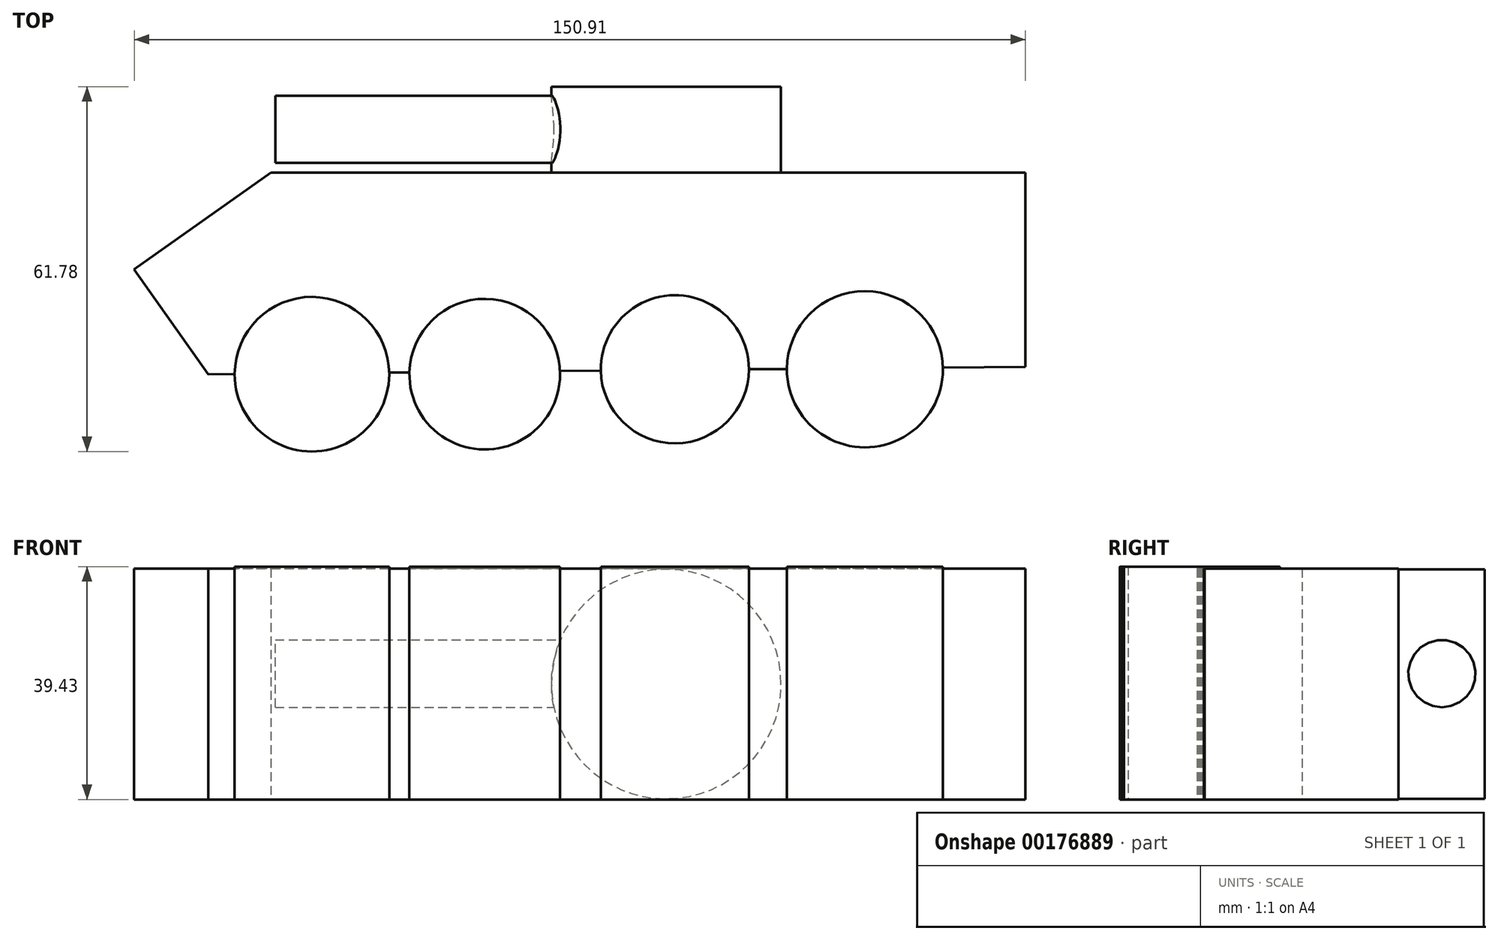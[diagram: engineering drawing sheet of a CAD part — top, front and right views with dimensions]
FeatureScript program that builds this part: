
annotation { "Feature Type Name" : "Feature", "Feature Type Description" : "" }
export const myFeature = defineFeature(function(context is Context, id is Id, definition is map)
    precondition{}
    {
        {
            var Q0;
            Q0=qCreatedBy(makeId("Top.planeOp"),FACE);
            var sketch = newSketch(context, id + "F0", { "sketchPlane" : qUnion([Q0])});
            skLineSegment(sketch, "E0", {"start": v(-76.08, 0) * mm, "end": v(-63.54, -17.77) * mm});
            skLineSegment(sketch, "E1", {"start": v(-63.54, -17.77) * mm, "end": v(-76.08, 0) * mm});
            skLineSegment(sketch, "E2", {"start": v(-76.08, 0) * mm, "end": v(-52.93, 16.35) * mm});
            skLineSegment(sketch, "E3", {"start": v(-52.93, 16.35) * mm, "end": v(74.83, 16.35) * mm});
            skLineSegment(sketch, "E4", {"start": v(74.83, 16.35) * mm, "end": v(74.83, -16.51) * mm});
            skLineSegment(sketch, "E5", {"start": v(74.83, -16.51) * mm, "end": v(-63.54, -17.77) * mm});
            skSolve(sketch);
        }
        {
            var Q0;
            Q0 = qSketchRegion(id + "F0", true);
            extrude(context, id + "F1", {"entities" : qUnion([Q0]), "depth" : 39.08 * mm});
        }
        {
            var Q0;
            Q0=qCreatedBy(makeId("Top.planeOp"),FACE);
            var sketch = newSketch(context, id + "F2", { "sketchPlane" : qUnion([Q0])});
            skCircle(sketch, "E6", {"center": v(-45.98, -17.77) * mm, "radius": 13.09 * mm});
            skCircle(sketch, "E7", {"center": v(-16.72, -17.77) * mm, "radius": 12.76 * mm});
            skCircle(sketch, "E8", {"center": v(15.47, -16.93) * mm, "radius": 12.54 * mm});
            skCircle(sketch, "E9", {"center": v(47.66, -16.93) * mm, "radius": 13.22 * mm});
            skSolve(sketch);
        }
        {
            var Q0;
            Q0 = qSketchRegion(id + "F2", true);
            extrude(context, id + "F3", {"entities" : qUnion([Q0]), "operationType" : NewBodyOperationType.ADD, "depth" : 39.43 * mm});
        }
        {
            var Q0;
            Q0=makeQuery(id+"F1.opExtrude","SWEPT_FACE",FACE,{"disambiguationData":[OSD([sQuery(id+"F0.wireOp",EDGE,"E3")])]});
            var sketch = newSketch(context, id + "F4", { "sketchPlane" : qUnion([Q0])});
            skCircle(sketch, "E10", {"center": v(-14.02, 19.54) * mm, "radius": 19.43 * mm});
            skPoint(sketch, "E10.centerSnap0", {"position": v(-74.83, 19.54) * mm});
            skSolve(sketch);
        }
        {
            var Q0;
            Q0 = qSketchRegion(id + "F4", true);
            extrude(context, id + "F5", {"entities" : qUnion([Q0]), "operationType" : NewBodyOperationType.ADD, "depth" : 14.58 * mm});
        }
        {
            var Q0;
            Q0=qCreatedBy(makeId("Right.planeOp"),FACE);
            var sketch = newSketch(context, id + "F6", { "sketchPlane" : qUnion([Q0])});
            skCircle(sketch, "E11", {"center": v(23.68, 21.32) * mm, "radius": 5.7 * mm});
            skSolve(sketch);
        }
        {
            var Q0;
            Q0 = qSketchRegion(id + "F6", true);
            extrude(context, id + "F7", {"entities" : qUnion([Q0]), "operationType" : NewBodyOperationType.ADD, "oppositeDirection" : true, "depth" : 52.2 * mm});
        }
    });
